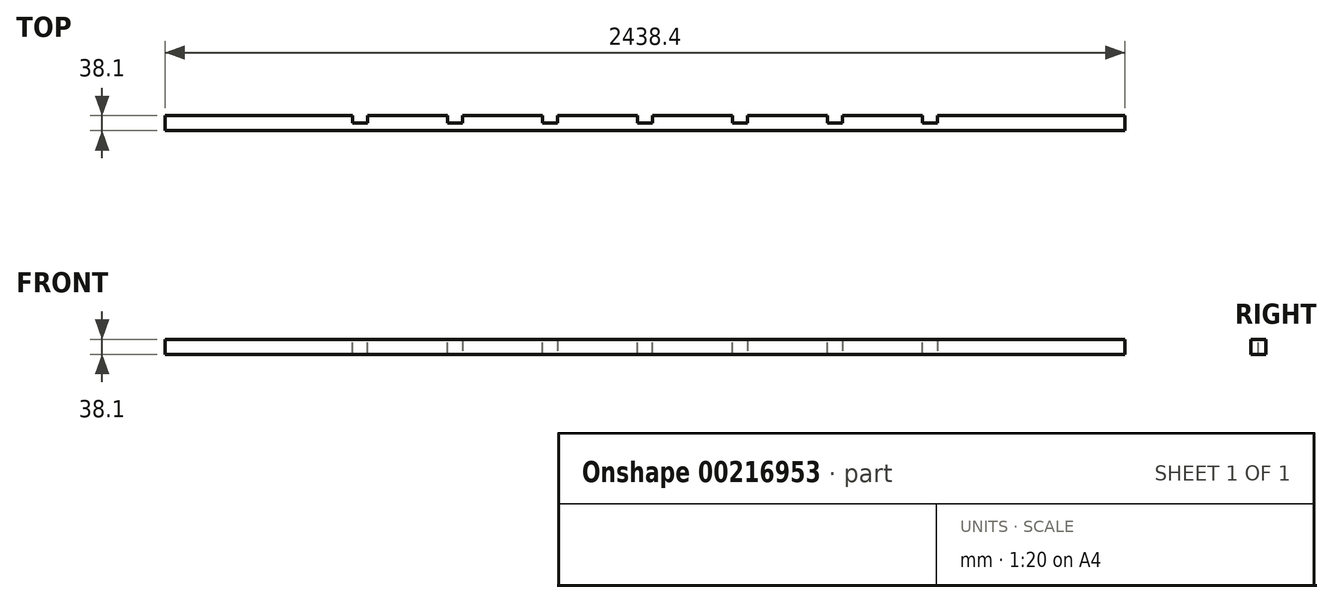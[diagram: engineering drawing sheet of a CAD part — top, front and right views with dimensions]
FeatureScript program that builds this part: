
annotation { "Feature Type Name" : "Feature", "Feature Type Description" : "" }
export const myFeature = defineFeature(function(context is Context, id is Id, definition is map)
    precondition{}
    {
        {
            var Q0;
            Q0=qCreatedBy(makeId("Top.planeOp"),FACE);
            var sketch = newSketch(context, id + "F0", { "sketchPlane" : qUnion([Q0])});
            skLineSegment(sketch, "E0", {"start": v(0, 0) * mm, "end": v(-76.26, 0) * mm});
            skLineSegment(sketch, "E1", {"start": v(-800.16, 0) * mm, "end": v(-800.16, 38.1) * mm});
            skLineSegment(sketch, "E2", {"start": v(-800.16, 38.1) * mm, "end": v(-596.96, 38.1) * mm});
            skLineSegment(sketch, "E3", {"start": v(0, 0) * mm, "end": v(126.94, 0) * mm});
            skLineSegment(sketch, "E4", {"start": v(126.94, 0) * mm, "end": v(126.94, 38.1) * mm});
            skLineSegment(sketch, "E5", {"start": v(165.04, 38.1) * mm, "end": v(165.04, 0) * mm});
            skLineSegment(sketch, "E6", {"start": v(165.04, 0) * mm, "end": v(368.24, 0) * mm});
            skLineSegment(sketch, "E7", {"start": v(368.24, 0) * mm, "end": v(368.24, 38.1) * mm});
            skLineSegment(sketch, "E8", {"start": v(406.34, 38.1) * mm, "end": v(406.34, 0) * mm});
            skLineSegment(sketch, "E9", {"start": v(406.34, 0) * mm, "end": v(609.54, 0) * mm});
            skLineSegment(sketch, "E10", {"start": v(609.54, 0) * mm, "end": v(609.54, 38.1) * mm});
            skLineSegment(sketch, "E11", {"start": v(647.64, 38.1) * mm, "end": v(647.64, 0) * mm});
            skLineSegment(sketch, "E12", {"start": v(647.64, 0) * mm, "end": v(1123.89, 0) * mm});
            skLineSegment(sketch, "E13", {"start": v(1123.89, 0) * mm, "end": v(1123.89, 38.1) * mm});
            skLineSegment(sketch, "E14", {"start": v(-76.26, 0) * mm, "end": v(-76.26, 38.1) * mm});
            skLineSegment(sketch, "E15", {"start": v(-838.26, 38.1) * mm, "end": v(-1314.51, 38.1) * mm});
            skLineSegment(sketch, "E16", {"start": v(-1314.51, 38.1) * mm, "end": v(-1314.51, 0) * mm});
            skLineSegment(sketch, "E17", {"start": v(-114.36, 0) * mm, "end": v(-114.36, 38.1) * mm});
            skLineSegment(sketch, "E18", {"start": v(-114.36, 38.1) * mm, "end": v(-317.56, 38.1) * mm});
            skLineSegment(sketch, "E19", {"start": v(-317.56, 38.1) * mm, "end": v(-317.56, 0) * mm});
            skLineSegment(sketch, "E20", {"start": v(-355.66, 0) * mm, "end": v(-355.66, 38.1) * mm});
            skLineSegment(sketch, "E21", {"start": v(-355.66, 38.1) * mm, "end": v(-558.86, 38.1) * mm});
            skLineSegment(sketch, "E22", {"start": v(-558.86, 38.1) * mm, "end": v(-558.86, 0) * mm});
            skLineSegment(sketch, "E23", {"start": v(-596.96, 0) * mm, "end": v(-596.96, 38.1) * mm});
            skLineSegment(sketch, "E24", {"start": v(-838.26, 0) * mm, "end": v(-838.26, 38.1) * mm});
            skLineSegment(sketch, "E25.trimOffspring", {"start": v(-558.86, 38.1) * mm, "end": v(-355.66, 38.1) * mm});
            skLineSegment(sketch, "E26.trimOffspring", {"start": v(-317.56, 38.1) * mm, "end": v(-114.36, 38.1) * mm});
            skLineSegment(sketch, "E27.trimOffspring", {"start": v(-1314.51, 38.1) * mm, "end": v(-838.26, 38.1) * mm});
            skLineSegment(sketch, "E28.trimOffspring", {"start": v(-596.96, 0) * mm, "end": v(-800.16, 0) * mm});
            skLineSegment(sketch, "E29.trimOffspring", {"start": v(-355.66, 0) * mm, "end": v(-558.86, 0) * mm});
            skLineSegment(sketch, "E30.trimOffspring", {"start": v(-114.36, 0) * mm, "end": v(-317.56, 0) * mm});
            skLineSegment(sketch, "E31.trimOffspring", {"start": v(-838.26, 0) * mm, "end": v(-1314.51, 0) * mm});
            skLineSegment(sketch, "E32.trimOffspring", {"start": v(-76.26, 38.1) * mm, "end": v(126.94, 38.1) * mm});
            skLineSegment(sketch, "E33.trimOffspring", {"start": v(126.94, 0) * mm, "end": v(0, 0) * mm});
            skLineSegment(sketch, "E34.trimOffspring", {"start": v(165.04, 38.1) * mm, "end": v(368.24, 38.1) * mm});
            skLineSegment(sketch, "E35.trimOffspring", {"start": v(368.24, 0) * mm, "end": v(165.04, 0) * mm});
            skLineSegment(sketch, "E36.trimOffspring", {"start": v(406.34, 38.1) * mm, "end": v(609.54, 38.1) * mm});
            skLineSegment(sketch, "E37.trimOffspring", {"start": v(609.54, 0) * mm, "end": v(406.34, 0) * mm});
            skLineSegment(sketch, "E38.trimOffspring", {"start": v(647.64, 38.1) * mm, "end": v(1123.89, 38.1) * mm});
            skLineSegment(sketch, "E39.trimOffspring", {"start": v(1123.89, 0) * mm, "end": v(647.64, 0) * mm});
            skSolve(sketch);
        }
        {
            var Q0;
            Q0=qSketchRegion(id+"F0",true);
            extrude(context, id + "F1", {"entities" : qUnion([Q0]), "depth" : 19.05 * mm});
        }
        {
            var Q0;
            Q0=makeQuery(id+"F1.opExtrude","CAP_FACE",FACE,{"disambiguationData":[OSD([sQuery(id+"F0.wireOp",EDGE,"E16"),sQuery(id+"F0.wireOp",EDGE,"E24"),sQuery(id+"F0.wireOp",EDGE,"E27.trimOffspring"),sQuery(id+"F0.wireOp",EDGE,"E31.trimOffspring")])],"isStart":false});
            var sketch = newSketch(context, id + "F2", { "sketchPlane" : qUnion([Q0])});
            skLineSegment(sketch, "E40.bottom", {"start": v(-1314.51, 38.1) * mm, "end": v(1123.89, 38.1) * mm});
            skLineSegment(sketch, "E40.top", {"start": v(-1314.51, 0) * mm, "end": v(1123.89, 0) * mm});
            skLineSegment(sketch, "E40.left", {"start": v(-1314.51, 38.1) * mm, "end": v(-1314.51, 0) * mm});
            skLineSegment(sketch, "E40.right", {"start": v(1123.89, 38.1) * mm, "end": v(1123.89, 0) * mm});
            skSolve(sketch);
        }
        {
            var Q0;
            Q0 = qSketchRegion(id + "F2", true);
            extrude(context, id + "F3", {"entities" : qUnion([Q0]), "depth" : 19.05 * mm});
        }
        {
            var Q0;
            Q0=makeQuery(id+"F3.opExtrude","SWEPT_BODY",BODY,{"disambiguationData":[OSD([sQuery(id+"F2.wireOp",EDGE,"E40.bottom"),sQuery(id+"F2.wireOp",EDGE,"E40.top"),sQuery(id+"F2.wireOp",EDGE,"E40.left"),sQuery(id+"F2.wireOp",EDGE,"E40.right")])]});
            var Q1;
            Q1=makeQuery(id+"F1.opExtrude","SWEPT_BODY",BODY,{"disambiguationData":[OSD([sQuery(id+"F0.wireOp",EDGE,"E1"),sQuery(id+"F0.wireOp",EDGE,"E2"),sQuery(id+"F0.wireOp",EDGE,"E23"),sQuery(id+"F0.wireOp",EDGE,"E28.trimOffspring")])]});
            var Q2;
            Q2=makeQuery(id+"F1.opExtrude","SWEPT_BODY",BODY,{"disambiguationData":[OSD([sQuery(id+"F0.wireOp",EDGE,"E4"),sQuery(id+"F0.wireOp",EDGE,"E0"),sQuery(id+"F0.wireOp",EDGE,"E14"),sQuery(id+"F0.wireOp",EDGE,"E32.trimOffspring"),sQuery(id+"F0.wireOp",EDGE,"E33.trimOffspring")])]});
            var Q3;
            Q3=makeQuery(id+"F1.opExtrude","SWEPT_BODY",BODY,{"disambiguationData":[OSD([sQuery(id+"F0.wireOp",EDGE,"E5"),sQuery(id+"F0.wireOp",EDGE,"E7"),sQuery(id+"F0.wireOp",EDGE,"E34.trimOffspring"),sQuery(id+"F0.wireOp",EDGE,"E35.trimOffspring")])]});
            var Q4;
            Q4=makeQuery(id+"F1.opExtrude","SWEPT_BODY",BODY,{"disambiguationData":[OSD([sQuery(id+"F0.wireOp",EDGE,"E8"),sQuery(id+"F0.wireOp",EDGE,"E10"),sQuery(id+"F0.wireOp",EDGE,"E36.trimOffspring"),sQuery(id+"F0.wireOp",EDGE,"E37.trimOffspring")])]});
            var Q5;
            Q5=makeQuery(id+"F1.opExtrude","SWEPT_BODY",BODY,{"disambiguationData":[OSD([sQuery(id+"F0.wireOp",EDGE,"E11"),sQuery(id+"F0.wireOp",EDGE,"E13"),sQuery(id+"F0.wireOp",EDGE,"E38.trimOffspring"),sQuery(id+"F0.wireOp",EDGE,"E39.trimOffspring")])]});
            var Q6;
            Q6=makeQuery(id+"F1.opExtrude","SWEPT_BODY",BODY,{"disambiguationData":[OSD([sQuery(id+"F0.wireOp",EDGE,"E16"),sQuery(id+"F0.wireOp",EDGE,"E24"),sQuery(id+"F0.wireOp",EDGE,"E27.trimOffspring"),sQuery(id+"F0.wireOp",EDGE,"E31.trimOffspring")])]});
            var Q7;
            Q7=makeQuery(id+"F1.opExtrude","SWEPT_BODY",BODY,{"disambiguationData":[OSD([sQuery(id+"F0.wireOp",EDGE,"E17"),sQuery(id+"F0.wireOp",EDGE,"E19"),sQuery(id+"F0.wireOp",EDGE,"E26.trimOffspring"),sQuery(id+"F0.wireOp",EDGE,"E30.trimOffspring")])]});
            var Q8;
            Q8=makeQuery(id+"F1.opExtrude","SWEPT_BODY",BODY,{"disambiguationData":[OSD([sQuery(id+"F0.wireOp",EDGE,"E20"),sQuery(id+"F0.wireOp",EDGE,"E22"),sQuery(id+"F0.wireOp",EDGE,"E25.trimOffspring"),sQuery(id+"F0.wireOp",EDGE,"E29.trimOffspring")])]});
            booleanBodies(context, id + "F4", {"operationType" : BooleanOperationType.UNION, "tools" : qUnion([Q0, Q1, Q2, Q3, Q4, Q5, Q6, Q7, Q8])});
        }
        {
            var Q0;
            Q0=makeQuery(id+"F3.opExtrude","SWEPT_BODY",BODY,{"disambiguationData":[OSD([sQuery(id+"F2.wireOp",EDGE,"E40.bottom"),sQuery(id+"F2.wireOp",EDGE,"E40.top"),sQuery(id+"F2.wireOp",EDGE,"E40.left"),sQuery(id+"F2.wireOp",EDGE,"E40.right")])]});
            var Q1;
            Q1=makeQuery(id+"F3.opExtrude","CAP_EDGE",EDGE,{"disambiguationData":[OSD([sQuery(id+"F2.wireOp",EDGE,"E40.top")])],"isStart":false});
            transform(context, id + "F5", {"entities" : qUnion([Q0]), "transformType" : TransformType.ROTATION, "transformAxis" : qUnion([Q1]), "angle" : 90 * degree, "makeCopy" : false});
        }
    });
